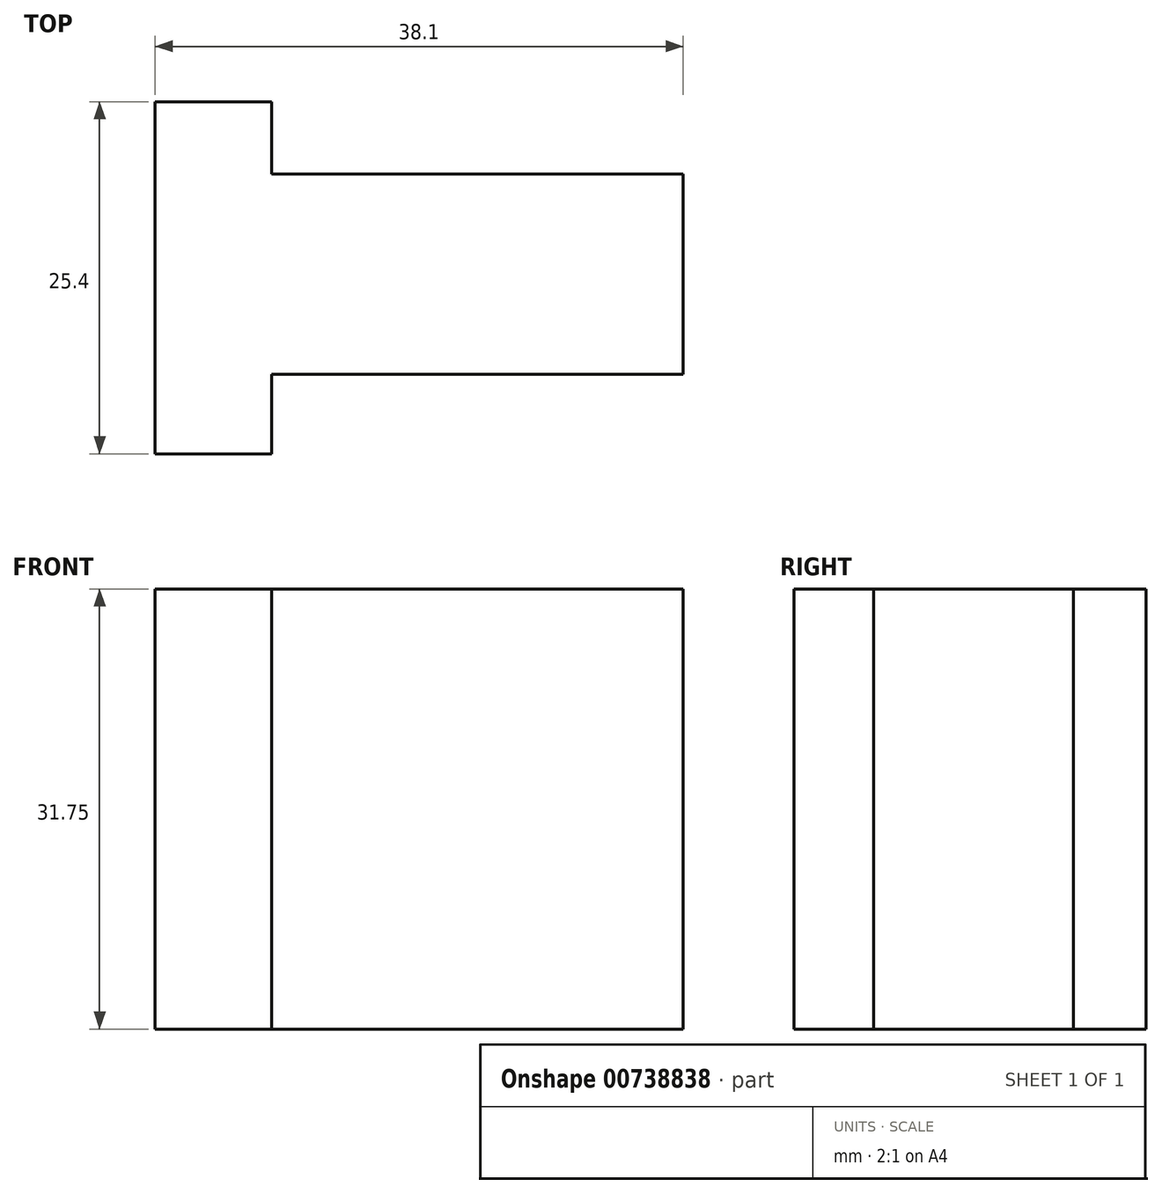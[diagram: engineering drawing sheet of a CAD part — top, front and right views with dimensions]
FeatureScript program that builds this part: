
annotation { "Feature Type Name" : "Feature", "Feature Type Description" : "" }
export const myFeature = defineFeature(function(context is Context, id is Id, definition is map)
    precondition{}
    {
        {
            var Q0;
            Q0=qCreatedBy(makeId("Front.planeOp"),FACE);
            var sketch = newSketch(context, id + "F0", { "sketchPlane" : qUnion([Q0])});
            skLineSegment(sketch, "E0", {"start": v(0, 0) * mm, "end": v(38.1, 0) * mm});
            skLineSegment(sketch, "E1", {"start": v(38.1, 0) * mm, "end": v(38.1, 31.75) * mm});
            skLineSegment(sketch, "E2", {"start": v(38.1, 31.75) * mm, "end": v(0, 31.75) * mm});
            skLineSegment(sketch, "E3", {"start": v(0, 31.75) * mm, "end": v(0, 0) * mm});
            skSolve(sketch);
        }
        {
            var Q0;
            Q0=makeQuery(id+"F0.imprint","IMPRINT",FACE,{"disambiguationData":[TD([[makeQuery(id+"F0.imprint","IMPRINT",EDGE,{"derivedFrom":sQuery(id+"F0.wireOp",EDGE,"E0")}),1.0]])]});
            extrude(context, id + "F1", {"entities" : qUnion([Q0]), "depth" : 25.4 * mm, "offsetDistance" : 25.4 * mm});
        }
        {
            var Q0;
            Q0=makeQuery(id+"F1.opExtrude","SWEPT_FACE",FACE,{"disambiguationData":[OSD([sQuery(id+"F0.wireOp",EDGE,"E2")])]});
            var sketch = newSketch(context, id + "F2", { "sketchPlane" : qUnion([Q0])});
            skLineSegment(sketch, "E4", {"start": v(8.4, -25.4) * mm, "end": v(8.4, -19.66) * mm});
            skLineSegment(sketch, "E5", {"start": v(8.4, -19.66) * mm, "end": v(38.1, -19.66) * mm});
            skLineSegment(sketch, "E6", {"start": v(38.1, -19.66) * mm, "end": v(38.1, -25.4) * mm});
            skLineSegment(sketch, "E7", {"start": v(38.1, -25.4) * mm, "end": v(8.4, -25.4) * mm});
            skLineSegment(sketch, "E8", {"start": v(8.4, 0) * mm, "end": v(8.4, -5.24) * mm});
            skLineSegment(sketch, "E9", {"start": v(8.4, -5.24) * mm, "end": v(38.1, -5.24) * mm});
            skLineSegment(sketch, "E10", {"start": v(38.1, -5.24) * mm, "end": v(38.1, 0) * mm});
            skLineSegment(sketch, "E11", {"start": v(38.1, 0) * mm, "end": v(8.4, 0) * mm});
            skSolve(sketch);
        }
        {
            var Q0;
            Q0=makeQuery(id+"F2.imprint","IMPRINT",FACE,{"disambiguationData":[TD([[makeQuery(id+"F2.imprint","IMPRINT",EDGE,{"derivedFrom":sQuery(id+"F2.wireOp",EDGE,"E8")}),1.0]])]});
            var Q1;
            Q1=makeQuery(id+"F2.imprint","IMPRINT",FACE,{"disambiguationData":[TD([[makeQuery(id+"F2.imprint","IMPRINT",EDGE,{"derivedFrom":sQuery(id+"F2.wireOp",EDGE,"E4")}),-1.0]])]});
            extrude(context, id + "F3", {"entities" : qUnion([Q0, Q1]), "operationType" : NewBodyOperationType.REMOVE, "endBound" : BoundingType.THROUGH_ALL, "oppositeDirection" : true, "depth" : 25.4 * mm, "offsetDistance" : 25.4 * mm});
        }
    });
